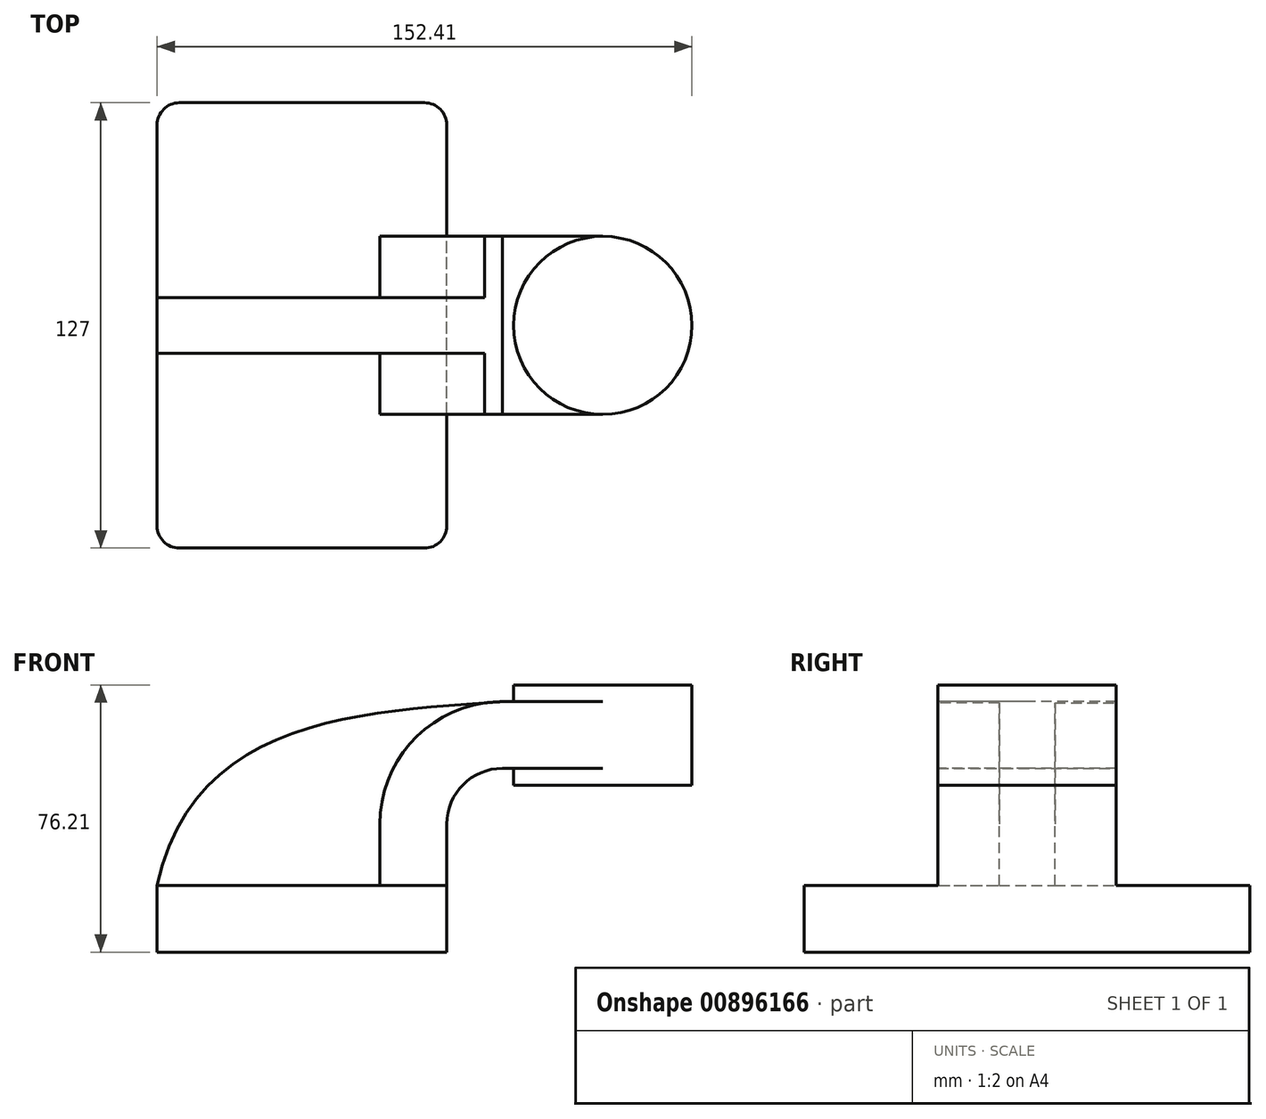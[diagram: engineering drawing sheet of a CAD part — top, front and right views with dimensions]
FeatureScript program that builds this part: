
annotation { "Feature Type Name" : "Feature", "Feature Type Description" : "" }
export const myFeature = defineFeature(function(context is Context, id is Id, definition is map)
    precondition{}
    {
        {
            var Q0;
            Q0=qCreatedBy(makeId("Front.planeOp"),FACE);
            var sketch = newSketch(context, id + "F0", { "sketchPlane" : qUnion([Q0])});
            skLineSegment(sketch, "E0.bottom", {"start": v(41.27, 9.53) * mm, "end": v(-41.28, 9.53) * mm});
            skLineSegment(sketch, "E0.top", {"start": v(41.28, -9.52) * mm, "end": v(-41.27, -9.52) * mm});
            skLineSegment(sketch, "E0.left", {"start": v(41.28, 9.53) * mm, "end": v(41.28, -9.52) * mm});
            skLineSegment(sketch, "E0.right", {"start": v(-41.28, 9.53) * mm, "end": v(-41.28, -9.52) * mm});
            skPoint(sketch, "E0.middle", {"position": v(0, 0) * mm});
            skLineSegment(sketch, "E1.bottom", {"start": v(111.12, 66.68) * mm, "end": v(60.32, 66.68) * mm});
            skLineSegment(sketch, "E1.top", {"start": v(111.12, 38.1) * mm, "end": v(60.32, 38.1) * mm});
            skLineSegment(sketch, "E1.left", {"start": v(111.12, 66.68) * mm, "end": v(111.12, 38.1) * mm});
            skLineSegment(sketch, "E1.right", {"start": v(60.32, 66.68) * mm, "end": v(60.32, 38.1) * mm});
            skPoint(sketch, "E1.middle", {"position": v(85.72, 52.39) * mm});
            skLineSegment(sketch, "E2", {"start": v(41.27, 9.53) * mm, "end": v(41.27, 27) * mm});
            skArc(sketch, "E3", {"start": v(41.27, 27) * mm, "mid": v(45.92, 38.23) * mm, "end": v(57.15, 42.88) * mm});
            skLineSegment(sketch, "E4", {"start": v(57.15, 42.88) * mm, "end": v(73.37, 42.88) * mm});
            skLineSegment(sketch, "E5.0", {"start": v(57.15, 61.93) * mm, "end": v(73.37, 61.93) * mm});
            skArc(sketch, "E5.1", {"start": v(22.22, 27) * mm, "mid": v(32.45, 51.7) * mm, "end": v(57.15, 61.93) * mm});
            skLineSegment(sketch, "E5.2", {"start": v(22.23, 9.53) * mm, "end": v(22.23, 27) * mm});
            skLineSegment(sketch, "E6", {"start": v(85.72, 38.1) * mm, "end": v(85.72, 66.68) * mm});
            skLineSegment(sketch, "E7", {"start": v(73.37, 42.88) * mm, "end": v(85.72, 42.88) * mm});
            skLineSegment(sketch, "E8", {"start": v(85.72, 42.88) * mm, "end": v(85.72, 61.93) * mm});
            skLineSegment(sketch, "E9", {"start": v(85.72, 61.93) * mm, "end": v(73.37, 61.93) * mm});
            skFitSpline(sketch, "E10", {"points": [v(-41.28, 9.52) * mm, v(57.15, 61.93) * mm], "startDerivative": vector(32.13, 145.71) * mm, "endDerivative": vector(117.44, 8.97) * mm});
            skSolve(sketch);
        }
        {
            var Q0;
            Q0=makeQuery(id+"F0.imprint","IMPRINT",FACE,{"disambiguationData":[TD([[makeQuery(id+"F0.imprint","IMPRINT",EDGE,{"derivedFrom":sQuery(id+"F0.wireOp",EDGE,"E0.top")}),-1.0]])]});
            extrude(context, id + "F1", {"entities" : qUnion([Q0]), "endBound" : BoundingType.SYMMETRIC, "depth" : 127 * mm, "offsetDistance" : 25.4 * mm});
        }
        {
            var Q0;
            {var subQ1=sQuery(id+"F0.wireOp",EDGE,"E2");Q0=makeQuery(id+"F0.imprint","IMPRINT",FACE,{"disambiguationData":[TD([[makeQuery(id+"F0.imprint","IMPRINT",EDGE,{"derivedFrom":subQ1}),1.0]])]});}
            var Q1;
            {var subQ0=sQuery(id+"F0.wireOp",EDGE,"E7");Q1=makeQuery(id+"F0.imprint","IMPRINT",FACE,{"disambiguationData":[TD([[makeQuery(id+"F0.imprint","IMPRINT",EDGE,{"derivedFrom":subQ0}),1.0]])]});}
            extrude(context, id + "F2", {"entities" : qUnion([Q0, Q1]), "operationType" : NewBodyOperationType.ADD, "endBound" : BoundingType.SYMMETRIC, "depth" : 50.8 * mm, "offsetDistance" : 25.4 * mm});
        }
        {
            var Q0;
            {var subQ3=sQuery(id+"F0.wireOp",EDGE,"E5.2");Q0=makeQuery(id+"F0.imprint","IMPRINT",FACE,{"disambiguationData":[TD([[makeQuery(id+"F0.imprint","IMPRINT",EDGE,{"derivedFrom":subQ3}),1.0]])]});}
            extrude(context, id + "F3", {"entities" : qUnion([Q0]), "operationType" : NewBodyOperationType.ADD, "endBound" : BoundingType.SYMMETRIC, "depth" : 15.88 * mm, "offsetDistance" : 25.4 * mm});
        }
        {
            var Q0;
            {var subQ0=sQuery(id+"F0.wireOp",EDGE,"E1.left");Q0=makeQuery(id+"F0.imprint","IMPRINT",FACE,{"disambiguationData":[TD([[makeQuery(id+"F0.imprint","IMPRINT",EDGE,{"derivedFrom":subQ0}),-1.0]])]});}
            var Q1;
            Q1=sQuery(id+"F0.wireOp",EDGE,"E6");
            revolve(context, id + "F4", {"operationType" : NewBodyOperationType.ADD, "surfaceOperationType" : NewSurfaceOperationType.NEW, "entities" : qUnion([Q0]), "axis" : qUnion([Q1]), "revolveType" : RevolveType.FULL});
        }
        {
            var Q0;
            Q0=makeQuery(id+"F1.opExtrude","CAP_EDGE",EDGE,{"disambiguationData":[OSD([sQuery(id+"F0.wireOp",EDGE,"E0.left")])],"isStart":false});
            var Q1;
            Q1=makeQuery(id+"F1.opExtrude","CAP_EDGE",EDGE,{"disambiguationData":[OSD([sQuery(id+"F0.wireOp",EDGE,"E0.right")])],"isStart":false});
            var Q2;
            Q2=makeQuery(id+"F1.opExtrude","CAP_EDGE",EDGE,{"disambiguationData":[OSD([sQuery(id+"F0.wireOp",EDGE,"E0.right")])],"isStart":true});
            var Q3;
            Q3=makeQuery(id+"F1.opExtrude","CAP_EDGE",EDGE,{"disambiguationData":[OSD([sQuery(id+"F0.wireOp",EDGE,"E0.left")])],"isStart":true});
            fillet(context, id + "F5", {"entities" : qUnion([Q0, Q1, Q2, Q3]), "radius" : 6.35 * mm, "tangentPropagation" : true, "allowEdgeOverflow" : false});
        }
    });
